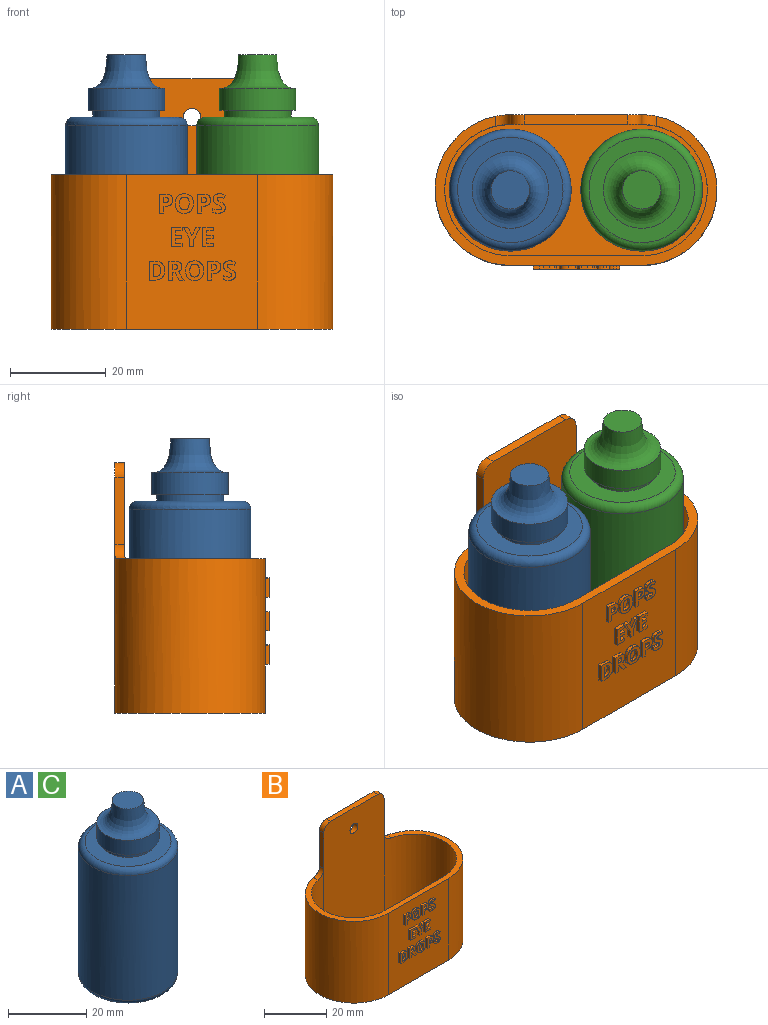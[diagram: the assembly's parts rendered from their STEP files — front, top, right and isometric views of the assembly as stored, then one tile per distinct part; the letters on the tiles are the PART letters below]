
ASSEMBLY  parts=3 mates=2
PART A: 10 faces, bbox 27.5x27.5x55.4 mm
  f0: plane 22x22mm, normal (0,0,1), area 226.2mm2, adj f7,f8
  f1: cylinder r=12.7mm len=39.02mm, axis (0,0,1), area 3113.5mm2, adj f8,f9
  f2: plane 22x22mm, normal (0,0,-1), area 380.1mm2, adj f9
  f3: plane 8x8mm, normal (0,0,1), area 50.3mm2, adj f4
  f4: revolved ~16x16mm, area 291.1mm2, adj f3,f5
  f5: cylinder r=8mm len=16mm, axis (0,0,1), area 231.2mm2, adj f4,f6
  f6: plane 16x16mm, normal (0,0,-1), area 47.1mm2, adj f5,f7
  f7: cylinder r=7mm len=14mm, axis (0,0,1), area 61.6mm2, adj f0,f6
  f8: torus R=11mm, axis (0,0,-1), area 202.7mm2, adj f0,f1
  f9: torus R=11mm, axis (0,0,1), area 202.7mm2, adj f1,f2
PART B: 234 faces, bbox 58.8x32.2x52.2 mm
  f0: plane 32.22x27.4mm, normal (0,-1,0), area 785mm2, adj f1,f6,f7,f10,f19,f20,f21,f22
  f1: plane 58.8x31.11mm, normal (0,0,1), area 227.4mm2, adj f0,f2,f4,f6,f7,f8,f15,f16
  f2: cylinder r=13.7mm len=33.42mm, axis (0,0,-1), area 1311.1mm2, adj f1,f3,f8,f9,f15
  f3: plane 50.42x27.4mm, normal (0,-1,0), area 1367.1mm2, adj f2,f4,f9,f11,f12,f13,f14,f17
  f4: cylinder r=13.7mm len=33.42mm, axis (0,0,-1), area 1311.1mm2, adj f1,f3,f8,f9,f16
  f5: plane 52.22x27.4mm, normal (0,1,0), area 1416.4mm2, adj f6,f7,f10,f11,f12,f13,f14,f17
  f6: cylinder r=15.7mm len=35.22mm, axis (0,0,-1), area 1591mm2, adj f0,f1,f5,f10,f15
  f7: cylinder r=15.7mm len=35.22mm, axis (0,0,-1), area 1591mm2, adj f0,f1,f5,f10,f16
  f8: plane 30.42x27.4mm, normal (0,1,0), area 833.5mm2, adj f1,f2,f4,f9
  f9: plane 54.8x27.4mm, normal (0,0,1), area 1340.4mm2, adj f2,f3,f4,f8
  f10: plane 58.8x31.4mm, normal (0,0,-1), area 1634.7mm2, adj f0,f5,f6,f7
  f11: plane 14x2mm, normal (-1,0,0), area 28mm2, adj f3,f5,f15,f17
  f12: plane 14x2mm, normal (1,0,0), area 28mm2, adj f3,f5,f16,f18
  f13: plane 21.4x2mm, normal (0,0,1), area 42.8mm2, adj f3,f5,f17,f18
  f14: cylinder r=1.83mm len=3.66mm, axis (0,-1,0), area 23mm2, adj f3,f5
  f15: cylinder r=3mm len=3mm, axis (0,-1,0), area 9.5mm2, adj f1,f2,f6,f11
  f16: cylinder r=3mm len=3mm, axis (0,1,0), area 9.5mm2, adj f1,f4,f7,f12
  f17: cylinder r=3mm len=3mm, axis (0,1,0), area 9.4mm2, adj f3,f5,f11,f13
  f18: cylinder r=3mm len=3mm, axis (0,-1,0), area 9.4mm2, adj f3,f5,f12,f13
  f19: extruded ~0.98x0.8mm, area 0.9mm2, adj f0,f20,f34,f35
  f20: extruded ~0.93x0.8mm, area 0.8mm2, adj f0,f19,f21,f35
  f21: extruded ~1.1x0.8mm, area 0.9mm2, adj f0,f20,f22,f35
  f22: plane 1.27x0.8mm, normal (0,0,1), area 1mm2, adj f0,f21,f23,f35
  f23: plane 3.97x0.8mm, normal (-1,0,0), area 3.2mm2, adj f0,f22,f24,f35
  f24: plane 0.84x0.8mm, normal (0,0,-1), area 0.7mm2, adj f0,f23,f25,f35
  f25: plane 1.41x0.8mm, normal (1,0,0), area 1.1mm2, adj f0,f24,f26,f35
  f26: plane 0.8x0.36mm, normal (0,0,-1), area 0.3mm2, adj f0,f25,f34,f35
  f27: plane 0.8x0.28mm, normal (0,0,1), area 0.2mm2, adj f28,f33,f35,f36
  f28: plane 1.18x0.8mm, normal (1,0,0), area 0.9mm2, adj f27,f29,f35,f36
  f29: plane 0.8x0.38mm, normal (0,0,-1), area 0.3mm2, adj f28,f30,f35,f36
  f30: extruded ~0.8x0.51mm, area 0.4mm2, adj f29,f31,f35,f36
  f31: extruded ~0.8x0.44mm, area 0.4mm2, adj f30,f32,f35,f36
  f32: extruded ~0.8x0.45mm, area 0.4mm2, adj f31,f33,f35,f36
  f33: extruded ~0.8x0.58mm, area 0.5mm2, adj f27,f32,f35,f36
  f34: extruded ~1.14x0.8mm, area 1mm2, adj f0,f19,f26,f35
  f35: plane 3.97x2.74mm, normal (0,-1,0), area 6.4mm2, adj f19,f20,f21,f22,f23,f24,f25,f26
  f36: plane 1.18x1.05mm, normal (0,-1,0), area 1.1mm2, adj f27,f28,f29,f30,f31,f32,f33
  f37: extruded ~1x0.8mm, area 0.8mm2, adj f38,f50,f51,f52
  f38: extruded ~1x0.8mm, area 0.8mm2, adj f37,f39,f51,f52
  f39: extruded ~0.8x0.76mm, area 0.7mm2, adj f38,f40,f51,f52
  f40: extruded ~1.34x1mm, area 1.5mm2, adj f39,f41,f51,f52
  f41: extruded ~1.34x1.01mm, area 1.5mm2, adj f40,f50,f51,f52
  f42: extruded ~1.51x0.8mm, area 1.3mm2, adj f0,f43,f49,f51
  f43: extruded ~1.51x0.8mm, area 1.3mm2, adj f0,f42,f44,f51
  f44: extruded ~1.4x0.8mm, area 1.2mm2, adj f0,f43,f45,f51
  f45: extruded ~1.4x0.8mm, area 1.2mm2, adj f0,f44,f46,f51
  f46: extruded ~1.51x0.8mm, area 1.3mm2, adj f0,f45,f47,f51
  f47: extruded ~1.52x0.8mm, area 1.3mm2, adj f0,f46,f48,f51
  f48: extruded ~1.4x0.8mm, area 1.2mm2, adj f0,f47,f49,f51
  f49: extruded ~1.4x0.8mm, area 1.2mm2, adj f0,f42,f48,f51
  f50: extruded ~0.8x0.75mm, area 0.7mm2, adj f37,f41,f51,f52
  f51: plane 4.08x3.78mm, normal (0,-1,0), area 8.2mm2, adj f37,f38,f39,f40,f41,f42,f43,f44
  f52: plane 2.68x2.01mm, normal (0,-1,0), area 4.5mm2, adj f37,f38,f39,f40,f41,f50
  f53: extruded ~0.98x0.8mm, area 0.9mm2, adj f0,f54,f68,f69
  f54: extruded ~0.93x0.8mm, area 0.8mm2, adj f0,f53,f55,f69
  f55: extruded ~1.1x0.8mm, area 0.9mm2, adj f0,f54,f56,f69
  f56: plane 1.27x0.8mm, normal (0,0,1), area 1mm2, adj f0,f55,f57,f69
  f57: plane 3.97x0.8mm, normal (-1,0,0), area 3.2mm2, adj f0,f56,f58,f69
  f58: plane 0.84x0.8mm, normal (0,0,-1), area 0.7mm2, adj f0,f57,f59,f69
  f59: plane 1.41x0.8mm, normal (1,0,0), area 1.1mm2, adj f0,f58,f60,f69
  f60: plane 0.8x0.36mm, normal (0,0,-1), area 0.3mm2, adj f0,f59,f68,f69
  f61: plane 0.8x0.28mm, normal (0,0,1), area 0.2mm2, adj f62,f67,f69,f70
  f62: plane 1.18x0.8mm, normal (1,0,0), area 0.9mm2, adj f61,f63,f69,f70
  f63: plane 0.8x0.38mm, normal (0,0,-1), area 0.3mm2, adj f62,f64,f69,f70
  f64: extruded ~0.8x0.51mm, area 0.4mm2, adj f63,f65,f69,f70
  f65: extruded ~0.8x0.44mm, area 0.4mm2, adj f64,f66,f69,f70
  f66: extruded ~0.8x0.45mm, area 0.4mm2, adj f65,f67,f69,f70
  f67: extruded ~0.8x0.58mm, area 0.5mm2, adj f61,f66,f69,f70
  f68: extruded ~1.14x0.8mm, area 1mm2, adj f0,f53,f60,f69
  f69: plane 3.97x2.74mm, normal (0,-1,0), area 6.4mm2, adj f53,f54,f55,f56,f57,f58,f59,f60
  f70: plane 1.18x1.05mm, normal (0,-1,0), area 1.1mm2, adj f61,f62,f63,f64,f65,f66,f67
  f71: extruded ~0.85x0.8mm, area 0.8mm2, adj f0,f72,f98,f99
  f72: extruded ~0.8x0.66mm, area 0.6mm2, adj f0,f71,f73,f99
  f73: extruded ~0.8x0.76mm, area 0.8mm2, adj f0,f72,f74,f99
  f74: extruded ~0.8x0.53mm, area 0.5mm2, adj f0,f73,f75,f99
  f75: extruded ~0.8x0.16mm, area 0.2mm2, adj f0,f74,f76,f99
  f76: extruded ~0.8x0.19mm, area 0.2mm2, adj f0,f75,f77,f99
  f77: extruded ~0.8x0.29mm, area 0.3mm2, adj f0,f76,f78,f99
  f78: extruded ~0.8x0.37mm, area 0.3mm2, adj f0,f77,f79,f99
  f79: extruded ~0.8x0.41mm, area 0.3mm2, adj f0,f78,f80,f99
  f80: extruded ~0.8x0.53mm, area 0.4mm2, adj f0,f79,f81,f99
  f81: plane 0.8x0.65mm, normal (0.92,0,-0.38), area 0.6mm2, adj f0,f80,f82,f99
  f82: extruded ~0.8x0.59mm, area 0.5mm2, adj f0,f81,f83,f99
  f83: extruded ~0.8x0.59mm, area 0.5mm2, adj f0,f82,f84,f99
  f84: extruded ~0.99x0.8mm, area 0.8mm2, adj f0,f83,f85,f99
  f85: extruded ~0.83x0.8mm, area 0.7mm2, adj f0,f84,f86,f99
  f86: extruded ~0.8x0.49mm, area 0.4mm2, adj f0,f85,f87,f99
  f87: extruded ~0.8x0.37mm, area 0.4mm2, adj f0,f86,f88,f99
  f88: extruded ~0.8x0.54mm, area 0.5mm2, adj f0,f87,f89,f99
  f89: extruded ~0.8x0.51mm, area 0.5mm2, adj f0,f88,f90,f99
  f90: extruded ~0.8x0.19mm, area 0.2mm2, adj f0,f89,f91,f99
  f91: extruded ~0.8x0.21mm, area 0.2mm2, adj f0,f90,f92,f99
  f92: extruded ~0.8x0.31mm, area 0.3mm2, adj f0,f91,f93,f99
  f93: extruded ~0.8x0.42mm, area 0.4mm2, adj f0,f92,f94,f99
  f94: extruded ~0.8x0.51mm, area 0.4mm2, adj f0,f93,f95,f99
  f95: extruded ~0.8x0.68mm, area 0.6mm2, adj f0,f94,f96,f99
  f96: plane 0.8x0.78mm, normal (-1,0,0), area 0.6mm2, adj f0,f95,f97,f99
  f97: extruded ~1.12x0.8mm, area 0.9mm2, adj f0,f96,f98,f99
  f98: extruded ~1.08x0.8mm, area 0.9mm2, adj f0,f71,f97,f99
  f99: plane 4.08x2.59mm, normal (0,-1,0), area 5.9mm2, adj f71,f72,f73,f74,f75,f76,f77,f78
  f100: plane 2.28x0.8mm, normal (0,0,-1), area 1.8mm2, adj f0,f101,f111,f112
  f101: plane 0.8x0.69mm, normal (1,0,0), area 0.6mm2, adj f0,f100,f102,f112
  f102: plane 1.44x0.8mm, normal (0,0,1), area 1.2mm2, adj f0,f101,f103,f112
  f103: plane 1.02x0.8mm, normal (1,0,0), area 0.8mm2, adj f0,f102,f104,f112
  f104: plane 1.34x0.8mm, normal (0,0,-1), area 1.1mm2, adj f0,f103,f105,f112
  f105: plane 0.8x0.69mm, normal (1,0,0), area 0.6mm2, adj f0,f104,f106,f112
  f106: plane 1.34x0.8mm, normal (0,0,1), area 1.1mm2, adj f0,f105,f107,f112
  f107: plane 0.87x0.8mm, normal (1,0,0), area 0.7mm2, adj f0,f106,f108,f112
  f108: plane 1.44x0.8mm, normal (0,0,-1), area 1.2mm2, adj f0,f107,f109,f112
  f109: plane 0.8x0.69mm, normal (1,0,0), area 0.6mm2, adj f0,f108,f110,f112
  f110: plane 2.28x0.8mm, normal (0,0,1), area 1.8mm2, adj f0,f109,f111,f112
  f111: plane 3.97x0.8mm, normal (-1,0,0), area 3.2mm2, adj f0,f100,f110,f112
  f112: plane 3.97x2.28mm, normal (0,-1,0), area 6.3mm2, adj f100,f101,f102,f103,f104,f105,f106,f107
  f113: plane 1.63x0.83mm, normal (-0.89,0,0.45), area 1.5mm2, adj f0,f114,f121,f122
  f114: plane 1.63x0.82mm, normal (0.89,0,0.45), area 1.5mm2, adj f0,f113,f115,f122
  f115: plane 0.91x0.8mm, normal (0,0,1), area 0.7mm2, adj f0,f114,f116,f122
  f116: plane 2.45x1.32mm, normal (-0.88,0,-0.47), area 2.2mm2, adj f0,f115,f117,f122
  f117: plane 1.52x0.8mm, normal (-1,0,0), area 1.2mm2, adj f0,f116,f118,f122
  f118: plane 0.84x0.8mm, normal (0,0,-1), area 0.7mm2, adj f0,f117,f119,f122
  f119: plane 1.54x0.8mm, normal (1,0,0), area 1.2mm2, adj f0,f118,f120,f122
  f120: plane 2.42x1.32mm, normal (0.88,0,-0.48), area 2.2mm2, adj f0,f119,f121,f122
  f121: plane 0.91x0.8mm, normal (0,0,1), area 0.7mm2, adj f0,f113,f120,f122
  f122: plane 3.97x3.47mm, normal (0,-1,0), area 5.2mm2, adj f113,f114,f115,f116,f117,f118,f119,f120
  f123: plane 2.28x0.8mm, normal (0,0,-1), area 1.8mm2, adj f0,f124,f134,f135
  f124: plane 0.8x0.69mm, normal (1,0,0), area 0.6mm2, adj f0,f123,f125,f135
  f125: plane 1.44x0.8mm, normal (0,0,1), area 1.2mm2, adj f0,f124,f126,f135
  f126: plane 1.02x0.8mm, normal (1,0,0), area 0.8mm2, adj f0,f125,f127,f135
  f127: plane 1.34x0.8mm, normal (0,0,-1), area 1.1mm2, adj f0,f126,f128,f135
  f128: plane 0.8x0.69mm, normal (1,0,0), area 0.6mm2, adj f0,f127,f129,f135
  f129: plane 1.34x0.8mm, normal (0,0,1), area 1.1mm2, adj f0,f128,f130,f135
  f130: plane 0.87x0.8mm, normal (1,0,0), area 0.7mm2, adj f0,f129,f131,f135
  f131: plane 1.44x0.8mm, normal (0,0,-1), area 1.2mm2, adj f0,f130,f132,f135
  f132: plane 0.8x0.69mm, normal (1,0,0), area 0.6mm2, adj f0,f131,f133,f135
  f133: plane 2.28x0.8mm, normal (0,0,1), area 1.8mm2, adj f0,f132,f134,f135
  f134: plane 3.97x0.8mm, normal (-1,0,0), area 3.2mm2, adj f0,f123,f133,f135
  f135: plane 3.97x2.28mm, normal (0,-1,0), area 6.3mm2, adj f123,f124,f125,f126,f127,f128,f129,f130
  f136: extruded ~1.28x1.13mm, area 1.6mm2, adj f137,f147,f148,f149
  f137: extruded ~1.3x1.22mm, area 1.6mm2, adj f136,f138,f148,f149
  f138: plane 0.8x0.36mm, normal (0,0,1), area 0.3mm2, adj f137,f139,f148,f149
  f139: plane 2.58x0.8mm, normal (1,0,0), area 2.1mm2, adj f138,f147,f148,f149
  f140: extruded ~1.5x0.8mm, area 1.3mm2, adj f0,f141,f146,f148
  f141: extruded ~1.43x0.8mm, area 1.3mm2, adj f0,f140,f142,f148
  f142: extruded ~1.51x0.8mm, area 1.3mm2, adj f0,f141,f143,f148
  f143: plane 1.24x0.8mm, normal (0,0,1), area 1mm2, adj f0,f142,f144,f148
  f144: plane 3.97x0.8mm, normal (-1,0,0), area 3.2mm2, adj f0,f143,f145,f148
  f145: plane 1.12x0.8mm, normal (0,0,-1), area 0.9mm2, adj f0,f144,f146,f148
  f146: extruded ~1.61x0.8mm, area 1.4mm2, adj f0,f140,f145,f148
  f147: plane 0.8x0.45mm, normal (0,0,-1), area 0.4mm2, adj f136,f139,f148,f149
  f148: plane 3.97x3.29mm, normal (0,-1,0), area 8mm2, adj f136,f137,f138,f139,f140,f141,f142,f143
  f149: plane 2.58x1.58mm, normal (0,-1,0), area 3.6mm2, adj f136,f137,f138,f139,f147
  f150: plane 1.52x0.8mm, normal (1,0,0), area 1.2mm2, adj f0,f151,f168,f169
  f151: plane 0.8x0.45mm, normal (0,0,-1), area 0.4mm2, adj f0,f150,f152,f169
  f152: plane 1.52x0.95mm, normal (-0.85,0,-0.53), area 1.4mm2, adj f0,f151,f153,f169
  f153: plane 0.93x0.8mm, normal (0,0,-1), area 0.7mm2, adj f0,f152,f154,f169
  f154: extruded ~1.73x1.17mm, area 1.7mm2, adj f0,f153,f155,f169
  f155: extruded ~0.8x0.55mm, area 0.6mm2, adj f0,f154,f156,f169
  f156: extruded ~0.8x0.62mm, area 0.5mm2, adj f0,f155,f157,f169
  f157: extruded ~0.89x0.8mm, area 0.8mm2, adj f0,f156,f158,f169
  f158: extruded ~1.2x0.8mm, area 1mm2, adj f0,f157,f159,f169
  f159: plane 1.16x0.8mm, normal (0,0,1), area 0.9mm2, adj f0,f158,f160,f169
  f160: plane 3.97x0.8mm, normal (-1,0,0), area 3.2mm2, adj f0,f159,f168,f169
  f161: plane 0.8x0.27mm, normal (0,0,1), area 0.2mm2, adj f162,f167,f169,f170
  f162: plane 1.07x0.8mm, normal (1,0,0), area 0.9mm2, adj f161,f163,f169,f170
  f163: plane 0.8x0.26mm, normal (0,0,-1), area 0.2mm2, adj f162,f164,f169,f170
  f164: extruded ~0.8x0.6mm, area 0.5mm2, adj f163,f165,f169,f170
  f165: extruded ~0.8x0.4mm, area 0.4mm2, adj f164,f166,f169,f170
  f166: extruded ~0.8x0.42mm, area 0.4mm2, adj f165,f167,f169,f170
  f167: extruded ~0.8x0.59mm, area 0.5mm2, adj f161,f166,f169,f170
  f168: plane 0.84x0.8mm, normal (0,0,-1), area 0.7mm2, adj f0,f150,f160,f169
  f169: plane 3.97x3.17mm, normal (0,-1,0), area 7.7mm2, adj f150,f151,f152,f153,f154,f155,f156,f157
  f170: plane 1.07x1.05mm, normal (0,-1,0), area 1mm2, adj f161,f162,f163,f164,f165,f166,f167
  f171: extruded ~1x0.8mm, area 0.8mm2, adj f172,f184,f185,f186
  f172: extruded ~1x0.8mm, area 0.8mm2, adj f171,f173,f185,f186
  f173: extruded ~0.8x0.76mm, area 0.7mm2, adj f172,f174,f185,f186
  f174: extruded ~1.34x1mm, area 1.5mm2, adj f173,f175,f185,f186
  f175: extruded ~1.34x1.01mm, area 1.5mm2, adj f174,f184,f185,f186
  f176: extruded ~1.51x0.8mm, area 1.3mm2, adj f0,f177,f183,f185
  f177: extruded ~1.51x0.8mm, area 1.3mm2, adj f0,f176,f178,f185
  f178: extruded ~1.4x0.8mm, area 1.2mm2, adj f0,f177,f179,f185
  f179: extruded ~1.4x0.8mm, area 1.2mm2, adj f0,f178,f180,f185
  f180: extruded ~1.51x0.8mm, area 1.3mm2, adj f0,f179,f181,f185
  f181: extruded ~1.52x0.8mm, area 1.3mm2, adj f0,f180,f182,f185
  f182: extruded ~1.4x0.8mm, area 1.2mm2, adj f0,f181,f183,f185
  f183: extruded ~1.4x0.8mm, area 1.2mm2, adj f0,f176,f182,f185
  f184: extruded ~0.8x0.75mm, area 0.7mm2, adj f171,f175,f185,f186
  f185: plane 4.08x3.78mm, normal (0,-1,0), area 8.2mm2, adj f171,f172,f173,f174,f175,f176,f177,f178
  f186: plane 2.68x2.01mm, normal (0,-1,0), area 4.5mm2, adj f171,f172,f173,f174,f175,f184
  f187: extruded ~0.98x0.8mm, area 0.9mm2, adj f0,f188,f202,f203
  f188: extruded ~0.93x0.8mm, area 0.8mm2, adj f0,f187,f189,f203
  f189: extruded ~1.1x0.8mm, area 0.9mm2, adj f0,f188,f190,f203
  f190: plane 1.27x0.8mm, normal (0,0,1), area 1mm2, adj f0,f189,f191,f203
  f191: plane 3.97x0.8mm, normal (-1,0,0), area 3.2mm2, adj f0,f190,f192,f203
  f192: plane 0.84x0.8mm, normal (0,0,-1), area 0.7mm2, adj f0,f191,f193,f203
  f193: plane 1.41x0.8mm, normal (1,0,0), area 1.1mm2, adj f0,f192,f194,f203
  f194: plane 0.8x0.36mm, normal (0,0,-1), area 0.3mm2, adj f0,f193,f202,f203
  f195: plane 0.8x0.28mm, normal (0,0,1), area 0.2mm2, adj f196,f201,f203,f204
  f196: plane 1.18x0.8mm, normal (1,0,0), area 0.9mm2, adj f195,f197,f203,f204
  f197: plane 0.8x0.38mm, normal (0,0,-1), area 0.3mm2, adj f196,f198,f203,f204
  f198: extruded ~0.8x0.51mm, area 0.4mm2, adj f197,f199,f203,f204
  f199: extruded ~0.8x0.44mm, area 0.4mm2, adj f198,f200,f203,f204
  f200: extruded ~0.8x0.45mm, area 0.4mm2, adj f199,f201,f203,f204
  f201: extruded ~0.8x0.58mm, area 0.5mm2, adj f195,f200,f203,f204
  f202: extruded ~1.14x0.8mm, area 1mm2, adj f0,f187,f194,f203
  f203: plane 3.97x2.74mm, normal (0,-1,0), area 6.4mm2, adj f187,f188,f189,f190,f191,f192,f193,f194
  f204: plane 1.18x1.05mm, normal (0,-1,0), area 1.1mm2, adj f195,f196,f197,f198,f199,f200,f201
  f205: extruded ~0.85x0.8mm, area 0.8mm2, adj f0,f206,f232,f233
  f206: extruded ~0.8x0.66mm, area 0.6mm2, adj f0,f205,f207,f233
  f207: extruded ~0.8x0.76mm, area 0.8mm2, adj f0,f206,f208,f233
  f208: extruded ~0.8x0.53mm, area 0.5mm2, adj f0,f207,f209,f233
  f209: extruded ~0.8x0.16mm, area 0.2mm2, adj f0,f208,f210,f233
  f210: extruded ~0.8x0.19mm, area 0.2mm2, adj f0,f209,f211,f233
  f211: extruded ~0.8x0.29mm, area 0.3mm2, adj f0,f210,f212,f233
  f212: extruded ~0.8x0.37mm, area 0.3mm2, adj f0,f211,f213,f233
  f213: extruded ~0.8x0.41mm, area 0.3mm2, adj f0,f212,f214,f233
  f214: extruded ~0.8x0.53mm, area 0.4mm2, adj f0,f213,f215,f233
  f215: plane 0.8x0.65mm, normal (0.92,0,-0.38), area 0.6mm2, adj f0,f214,f216,f233
  f216: extruded ~0.8x0.59mm, area 0.5mm2, adj f0,f215,f217,f233
  f217: extruded ~0.8x0.59mm, area 0.5mm2, adj f0,f216,f218,f233
  f218: extruded ~0.99x0.8mm, area 0.8mm2, adj f0,f217,f219,f233
  f219: extruded ~0.83x0.8mm, area 0.7mm2, adj f0,f218,f220,f233
  f220: extruded ~0.8x0.49mm, area 0.4mm2, adj f0,f219,f221,f233
  f221: extruded ~0.8x0.37mm, area 0.4mm2, adj f0,f220,f222,f233
  f222: extruded ~0.8x0.54mm, area 0.5mm2, adj f0,f221,f223,f233
  f223: extruded ~0.8x0.51mm, area 0.5mm2, adj f0,f222,f224,f233
  f224: extruded ~0.8x0.19mm, area 0.2mm2, adj f0,f223,f225,f233
  f225: extruded ~0.8x0.21mm, area 0.2mm2, adj f0,f224,f226,f233
  f226: extruded ~0.8x0.31mm, area 0.3mm2, adj f0,f225,f227,f233
  f227: extruded ~0.8x0.42mm, area 0.4mm2, adj f0,f226,f228,f233
  f228: extruded ~0.8x0.51mm, area 0.4mm2, adj f0,f227,f229,f233
  f229: extruded ~0.8x0.68mm, area 0.6mm2, adj f0,f228,f230,f233
  f230: plane 0.8x0.78mm, normal (-1,0,0), area 0.6mm2, adj f0,f229,f231,f233
  f231: extruded ~1.12x0.8mm, area 0.9mm2, adj f0,f230,f232,f233
  f232: extruded ~1.08x0.8mm, area 0.9mm2, adj f0,f205,f231,f233
  f233: plane 4.08x2.59mm, normal (0,-1,0), area 5.9mm2, adj f205,f206,f207,f208,f209,f210,f211,f212
PART C: same geometry as A
PLACE A rot(axis=(0,0,-1),90deg) t=(-13.7,0,1.8)mm
PLACE B t=(-13.7,0,1.8)mm
PLACE C rot(axis=(0,0,1),180deg) t=(13.7,0,1.8)mm
MATE slider A.f1 <-> B.f2  axis (0,0,-1) through (-13.7,0,1.8)mm
MATE slider C.f1 <-> B.f4  axis (0,0,-1) through (13.7,0,1.8)mm
